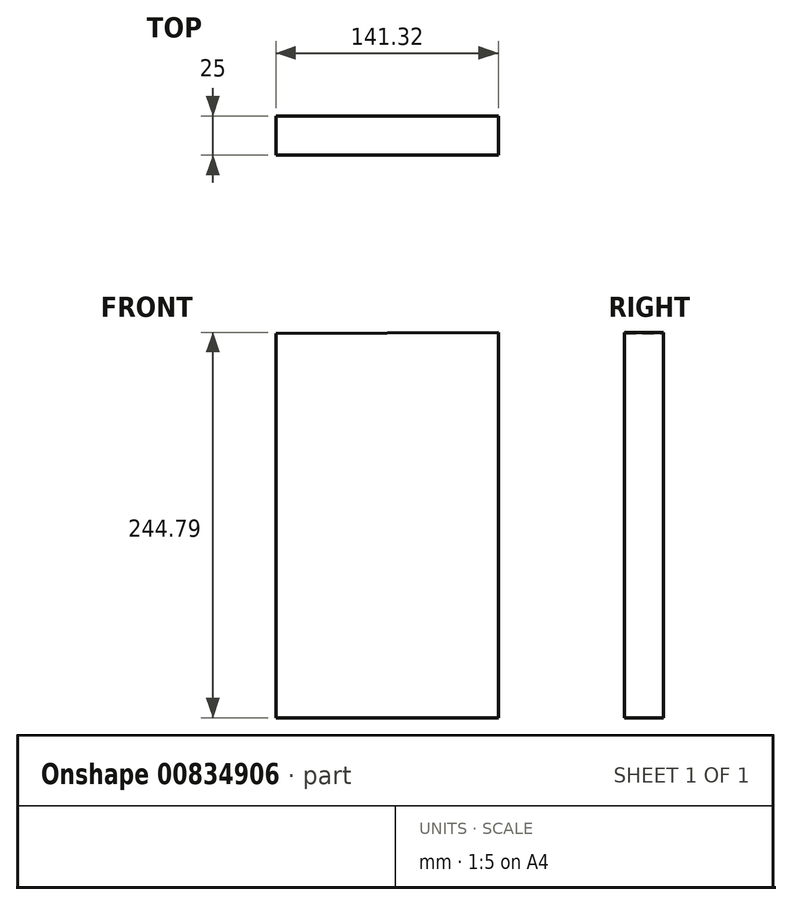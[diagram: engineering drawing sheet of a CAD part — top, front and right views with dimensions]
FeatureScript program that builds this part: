
annotation { "Feature Type Name" : "Feature", "Feature Type Description" : "" }
export const myFeature = defineFeature(function(context is Context, id is Id, definition is map)
    precondition{}
    {
        {
            var Q0;
            Q0=qCreatedBy(makeId("Front.planeOp"),FACE);
            var sketch = newSketch(context, id + "F0", { "sketchPlane" : qUnion([Q0])});
            skLineSegment(sketch, "E0", {"start": v(-74.2, 74.5) * mm, "end": v(-74.2, -169.63) * mm});
            skLineSegment(sketch, "E1", {"start": v(-74.2, -169.63) * mm, "end": v(67.13, -169.63) * mm});
            skLineSegment(sketch, "E2", {"start": v(67.13, -169.63) * mm, "end": v(67.13, 75.16) * mm});
            skLineSegment(sketch, "E3", {"start": v(67.13, 75.16) * mm, "end": v(-74.2, 74.5) * mm});
            skSolve(sketch);
        }
        {
            var Q0;
            Q0 = qSketchRegion(id + "F0", true);
            extrude(context, id + "F1", {"entities" : qUnion([Q0]), "depth" : 25 * mm, "offsetDistance" : 25 * mm});
        }
    });
